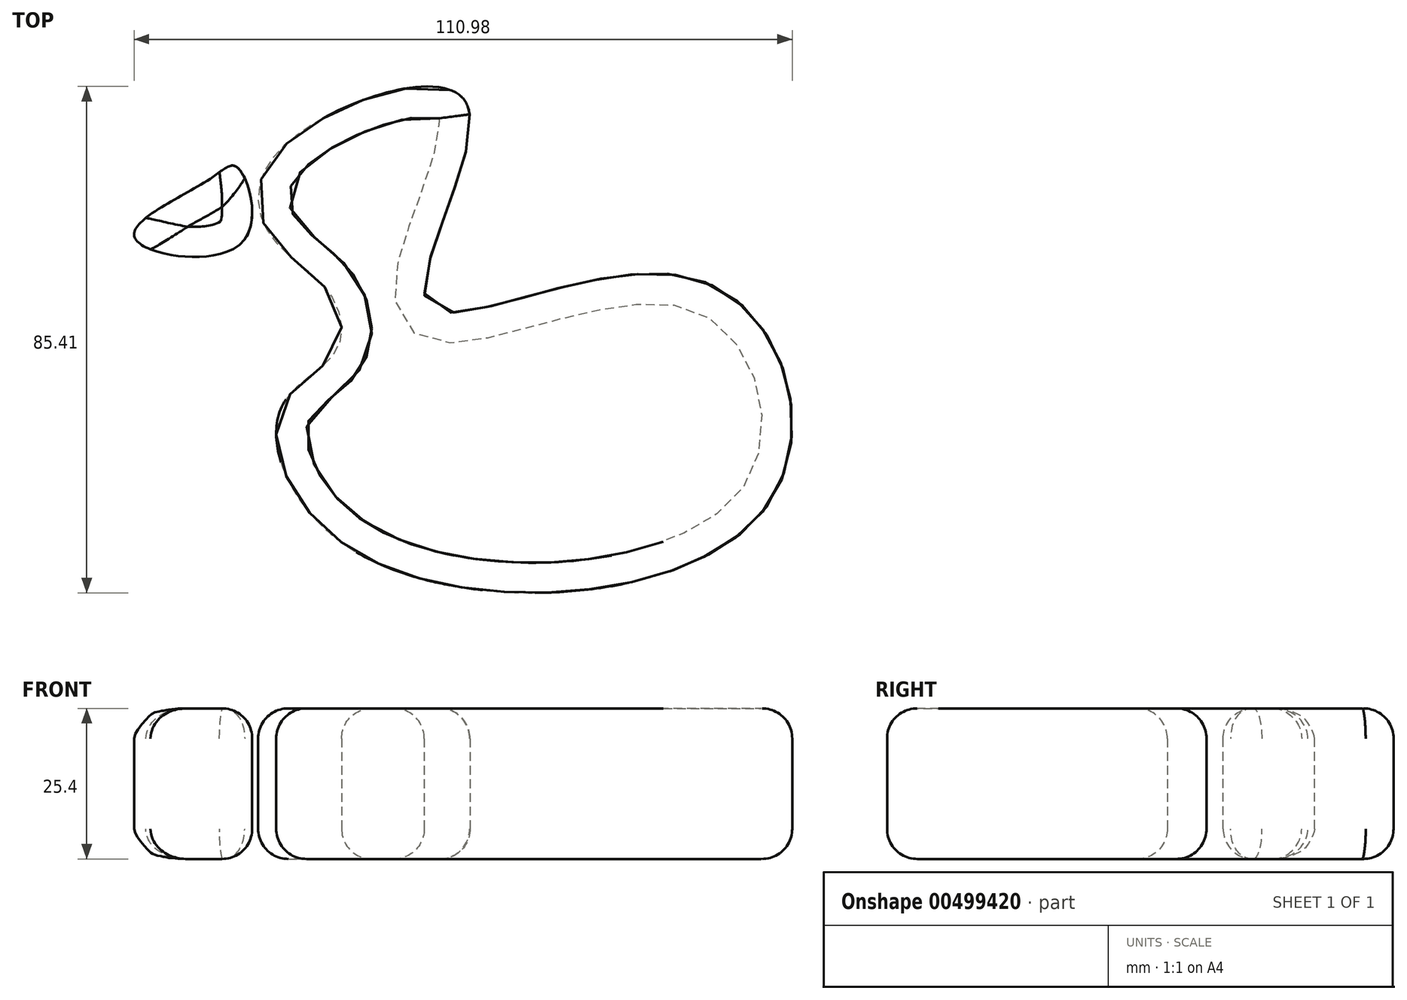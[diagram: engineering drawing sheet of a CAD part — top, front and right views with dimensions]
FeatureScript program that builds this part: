
annotation { "Feature Type Name" : "Feature", "Feature Type Description" : "" }
export const myFeature = defineFeature(function(context is Context, id is Id, definition is map)
    precondition{}
    {
        {
            var Q0;
            Q0=qCreatedBy(makeId("Top.planeOp"),FACE);
            var sketch = newSketch(context, id + "F0", { "sketchPlane" : qUnion([Q0])});
            skFitSpline(sketch, "E0", {"points": [v(-31.22, 28.74) * mm, v(0, 36.55) * mm, v(-6.56, 2.66) * mm, v(38.32, 6.92) * mm, v(51.1, -31.05) * mm, v(-17.03, -40.1) * mm, v(-31.22, -15.08) * mm, v(-22, -5.5) * mm, v(-23.06, 4.44) * mm, v(-33, 14.2) * mm, v(-31.22, 28.74) * mm]});
            skFitSpline(sketch, "E1", {"points": [v(-38.5, 25.55) * mm, v(-37.96, 12.77) * mm, v(-55.88, 13.84) * mm, v(-43.29, 23.6) * mm, v(-38.5, 25.55) * mm]});
            skSolve(sketch);
        }
        {
            var Q0;
            Q0=makeQuery(id+"F0.imprint","IMPRINT",FACE,{"disambiguationData":[TD([[makeQuery(id+"F0.imprint","IMPRINT",EDGE,{"derivedFrom":sQuery(id+"F0.wireOp",EDGE,"E1")}),-1.0]])]});
            var Q1;
            Q1=makeQuery(id+"F0.imprint","IMPRINT",FACE,{"disambiguationData":[TD([[makeQuery(id+"F0.imprint","IMPRINT",EDGE,{"derivedFrom":sQuery(id+"F0.wireOp",EDGE,"E0")}),-1.0]])]});
            extrude(context, id + "F1", {"entities" : qUnion([Q0, Q1]), "depth" : 25.4 * mm});
        }
        {
            var Q0;
            Q0=makeQuery(id+"F1.opExtrude","CAP_FACE",FACE,{"disambiguationData":[OSD([sQuery(id+"F0.wireOp",EDGE,"E0")])],"isStart":false});
            var Q1;
            Q1=makeQuery(id+"F1.opExtrude","CAP_FACE",FACE,{"disambiguationData":[OSD([sQuery(id+"F0.wireOp",EDGE,"E1")])],"isStart":false});
            var Q2;
            Q2=makeQuery(id+"F1.opExtrude","SWEPT_FACE",FACE,{"disambiguationData":[OSD([sQuery(id+"F0.wireOp",EDGE,"E1")])]});
            var Q3;
            Q3=makeQuery(id+"F1.opExtrude","CAP_FACE",FACE,{"disambiguationData":[OSD([sQuery(id+"F0.wireOp",EDGE,"E0")])],"isStart":true});
            var Q4;
            Q4=makeQuery(id+"F1.opExtrude","CAP_FACE",FACE,{"disambiguationData":[OSD([sQuery(id+"F0.wireOp",EDGE,"E1")])],"isStart":true});
            fillet(context, id + "F2", {"entities" : qUnion([Q0, Q1, Q2, Q3, Q4]), "radius" : 5.08 * mm, "tangentPropagation" : true, "allowEdgeOverflow" : false});
        }
    });
